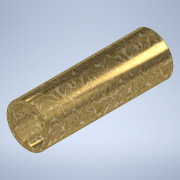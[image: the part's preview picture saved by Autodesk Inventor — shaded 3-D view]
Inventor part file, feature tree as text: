
AUTODESK INVENTOR PART (.ipt)
format: ipt  version: 2020 (Build 240168000, 168)  size: 135,168 bytes
history: native  units: mm
features: extrude x1, sketch x1
ambient origin geometry x8: Origin, YZ Plane, XZ Plane, XY Plane, X Axis, Y Axis, Z Axis, Center Point
bodies: Solid1 (feature_tree)
feature tree (2):
  extrude  "Extrusion1"  Depth=30.0mm
  sketch  "Sketch1"  dims[d0=10.0mm d1=8.0mm d2=30.0mm d3=0.0mm]
